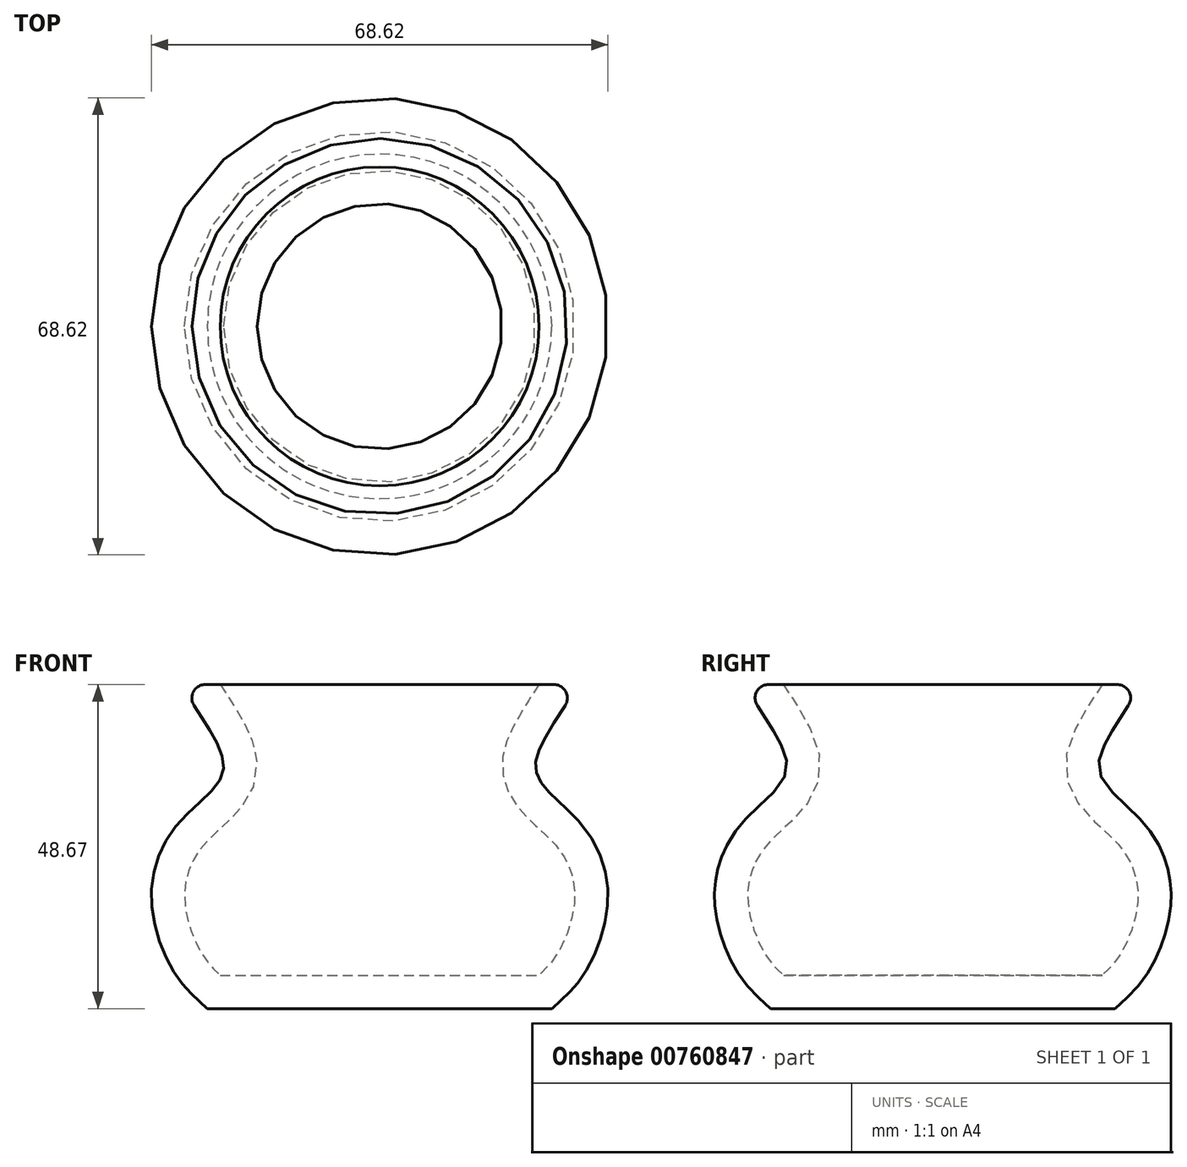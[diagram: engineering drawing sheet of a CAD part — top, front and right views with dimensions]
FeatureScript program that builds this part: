
annotation { "Feature Type Name" : "Feature", "Feature Type Description" : "" }
export const myFeature = defineFeature(function(context is Context, id is Id, definition is map)
    precondition{}
    {
        {
            var Q0;
            Q0=qCreatedBy(makeId("Front.planeOp"),FACE);
            var sketch = newSketch(context, id + "F0", { "sketchPlane" : qUnion([Q0])});
            skLineSegment(sketch, "E0", {"start": v(0, 0) * mm, "end": v(0, 49.68) * mm});
            skFitSpline(sketch, "E1", {"points": [v(31.27, 48.67) * mm, v(26.22, 42.95) * mm, v(23.52, 35.54) * mm, v(30.26, 27.79) * mm, v(34.3, 16.33) * mm, v(30.26, 4.54) * mm, v(25.88, 0) * mm], "startDerivative": vector(-44.81, -19.8) * mm, "endDerivative": vector(-27.66, -26.26) * mm});
            skLineSegment(sketch, "E2", {"start": v(31.27, 48.67) * mm, "end": v(0, 48.67) * mm});
            skLineSegment(sketch, "E3", {"start": v(25.88, 0) * mm, "end": v(0, 0) * mm});
            skSolve(sketch);
        }
        {
            var Q0;
            Q0=makeQuery(id+"F0.imprint","IMPRINT",FACE,{"disambiguationData":[TD([[makeQuery(id+"F0.imprint","IMPRINT",EDGE,{"derivedFrom":sQuery(id+"F0.wireOp",EDGE,"E1")}),-1.0]])]});
            var Q1;
            Q1=sQuery(id+"F0.wireOp",EDGE,"E0");
            revolve(context, id + "F1", {"surfaceOperationType" : NewSurfaceOperationType.NEW, "entities" : qUnion([Q0]), "axis" : qUnion([Q1]), "revolveType" : RevolveType.FULL});
        }
        {
            var Q0;
            Q0=makeQuery(id+"F1.opRevolve","SWEPT_EDGE",EDGE,{"disambiguationData":[OSD([sQuery(id+"F0.wireOp",EDGE,"E1"),sQuery(id+"F0.wireOp",EDGE,"E2")])]});
            fillet(context, id + "F2", {"entities" : qUnion([Q0]), "radius" : 2 * mm, "tangentPropagation" : true, "allowEdgeOverflow" : false});
        }
        {
            var Q0;
            Q0=makeQuery(id+"F1.opRevolve","SWEPT_FACE",FACE,{"disambiguationData":[OSD([sQuery(id+"F0.wireOp",EDGE,"E2")])]});
            shell(context, id + "F3", {"entities" : qUnion([Q0]), "thickness" : 5 * mm});
        }
    });
